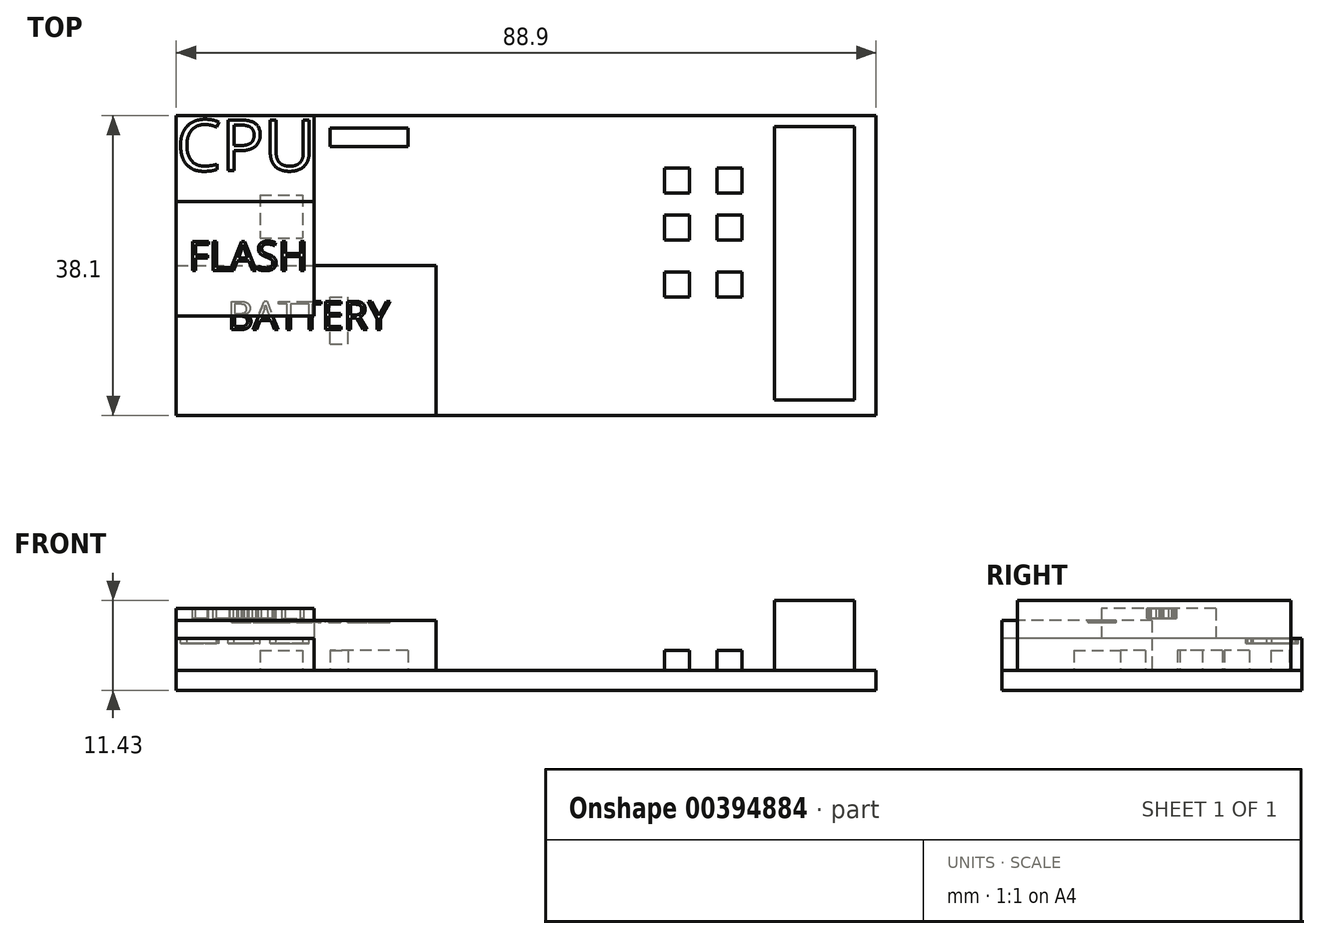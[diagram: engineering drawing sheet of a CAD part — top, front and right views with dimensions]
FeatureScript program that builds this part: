
annotation { "Feature Type Name" : "Feature", "Feature Type Description" : "" }
export const myFeature = defineFeature(function(context is Context, id is Id, definition is map)
    precondition{}
    {
        {
            var Q0;
            Q0=qCreatedBy(makeId("Top.planeOp"),FACE);
            var sketch = newSketch(context, id + "F0", { "sketchPlane" : qUnion([Q0])});
            skLineSegment(sketch, "E0.bottom", {"start": v(-84.59, -27.01) * mm, "end": v(4.31, -27.01) * mm});
            skLineSegment(sketch, "E0.top", {"start": v(-84.59, -65.11) * mm, "end": v(4.31, -65.11) * mm});
            skLineSegment(sketch, "E0.left", {"start": v(-84.59, -27.01) * mm, "end": v(-84.59, -65.11) * mm});
            skLineSegment(sketch, "E0.right", {"start": v(4.31, -27.01) * mm, "end": v(4.31, -65.11) * mm});
            skSolve(sketch);
        }
        {
            var Q0;
            Q0=makeQuery(id+"F0.imprint","IMPRINT",FACE,{"disambiguationData":[TD([[makeQuery(id+"F0.imprint","IMPRINT",EDGE,{"derivedFrom":sQuery(id+"F0.wireOp",EDGE,"E0.bottom")}),-1.0]])]});
            var sketch = newSketch(context, id + "F1", { "sketchPlane" : qUnion([Q0])});
            skLineSegment(sketch, "E1.bottom", {"start": v(-73.97, -37.1) * mm, "end": v(-68.53, -37.1) * mm});
            skLineSegment(sketch, "E1.top", {"start": v(-73.97, -42.55) * mm, "end": v(-68.53, -42.55) * mm});
            skLineSegment(sketch, "E1.left", {"start": v(-73.97, -37.1) * mm, "end": v(-73.97, -42.55) * mm});
            skLineSegment(sketch, "E1.right", {"start": v(-68.53, -37.1) * mm, "end": v(-68.53, -42.55) * mm});
            skLineSegment(sketch, "E2.bottom", {"start": v(-65.05, -56) * mm, "end": v(-62.74, -56) * mm});
            skLineSegment(sketch, "E2.top", {"start": v(-65.05, -50.1) * mm, "end": v(-62.74, -50.1) * mm});
            skLineSegment(sketch, "E2.left", {"start": v(-65.05, -56) * mm, "end": v(-65.05, -50.1) * mm});
            skLineSegment(sketch, "E2.right", {"start": v(-62.74, -56) * mm, "end": v(-62.74, -50.1) * mm});
            skLineSegment(sketch, "E3.bottom", {"start": v(-22.55, -33.7) * mm, "end": v(-19.38, -33.7) * mm});
            skLineSegment(sketch, "E3.top", {"start": v(-22.55, -36.88) * mm, "end": v(-19.38, -36.88) * mm});
            skLineSegment(sketch, "E3.left", {"start": v(-22.55, -33.7) * mm, "end": v(-22.55, -36.88) * mm});
            skLineSegment(sketch, "E3.right", {"start": v(-19.38, -33.7) * mm, "end": v(-19.38, -36.88) * mm});
            skLineSegment(sketch, "E4.bottom", {"start": v(-15.93, -36.88) * mm, "end": v(-12.75, -36.88) * mm});
            skLineSegment(sketch, "E4.top", {"start": v(-15.93, -33.7) * mm, "end": v(-12.75, -33.7) * mm});
            skLineSegment(sketch, "E4.left", {"start": v(-15.93, -36.88) * mm, "end": v(-15.93, -33.7) * mm});
            skLineSegment(sketch, "E4.right", {"start": v(-12.75, -36.88) * mm, "end": v(-12.75, -33.7) * mm});
            skLineSegment(sketch, "E5.bottom", {"start": v(-22.55, -39.69) * mm, "end": v(-19.38, -39.69) * mm});
            skLineSegment(sketch, "E5.top", {"start": v(-22.55, -42.86) * mm, "end": v(-19.38, -42.86) * mm});
            skLineSegment(sketch, "E5.left", {"start": v(-22.55, -39.69) * mm, "end": v(-22.55, -42.86) * mm});
            skLineSegment(sketch, "E5.right", {"start": v(-19.38, -39.69) * mm, "end": v(-19.38, -42.86) * mm});
            skLineSegment(sketch, "E6.bottom", {"start": v(-15.93, -42.86) * mm, "end": v(-12.75, -42.86) * mm});
            skLineSegment(sketch, "E6.top", {"start": v(-15.93, -39.69) * mm, "end": v(-12.75, -39.69) * mm});
            skLineSegment(sketch, "E6.left", {"start": v(-15.93, -42.86) * mm, "end": v(-15.93, -39.69) * mm});
            skLineSegment(sketch, "E6.right", {"start": v(-12.75, -42.86) * mm, "end": v(-12.75, -39.69) * mm});
            skLineSegment(sketch, "E7.bottom", {"start": v(-22.55, -46.92) * mm, "end": v(-19.38, -46.92) * mm});
            skLineSegment(sketch, "E7.top", {"start": v(-22.55, -50.1) * mm, "end": v(-19.38, -50.1) * mm});
            skLineSegment(sketch, "E7.left", {"start": v(-22.55, -46.92) * mm, "end": v(-22.55, -50.1) * mm});
            skLineSegment(sketch, "E7.right", {"start": v(-19.38, -46.92) * mm, "end": v(-19.38, -50.1) * mm});
            skLineSegment(sketch, "E8.bottom", {"start": v(-15.93, -46.92) * mm, "end": v(-12.75, -46.92) * mm});
            skLineSegment(sketch, "E8.top", {"start": v(-15.93, -50.1) * mm, "end": v(-12.75, -50.1) * mm});
            skLineSegment(sketch, "E8.left", {"start": v(-15.93, -46.92) * mm, "end": v(-15.93, -50.1) * mm});
            skLineSegment(sketch, "E8.right", {"start": v(-12.75, -46.92) * mm, "end": v(-12.75, -50.1) * mm});
            skPoint(sketch, "E9.oppositeSnap0", {"position": v(-65.05, -53.05) * mm});
            skLineSegment(sketch, "E9.bottom", {"start": v(-55.16, -30.95) * mm, "end": v(-65.05, -30.95) * mm});
            skLineSegment(sketch, "E9.top", {"start": v(-55.16, -28.6) * mm, "end": v(-65.05, -28.6) * mm});
            skLineSegment(sketch, "E9.left", {"start": v(-55.16, -30.95) * mm, "end": v(-55.16, -28.6) * mm});
            skLineSegment(sketch, "E9.right", {"start": v(-65.05, -30.95) * mm, "end": v(-65.05, -28.6) * mm});
            skSolve(sketch);
        }
        {
            var Q0;
            Q0 = qSketchRegion(id + "F1", true);
            extrude(context, id + "F2", {"entities" : qUnion([Q0]), "depth" : 2.54 * mm});
        }
        {
            var Q0;
            Q0 = qSketchRegion(id + "F0", true);
            extrude(context, id + "F3", {"entities" : qUnion([Q0]), "oppositeDirection" : true, "depth" : 2.54 * mm});
        }
        {
            var Q0;
            Q0=makeQuery(id+"F3.opExtrude","CAP_FACE",FACE,{"disambiguationData":[OSD([sQuery(id+"F0.wireOp",EDGE,"E0.bottom"),sQuery(id+"F0.wireOp",EDGE,"E0.top"),sQuery(id+"F0.wireOp",EDGE,"E0.left"),sQuery(id+"F0.wireOp",EDGE,"E0.right")])],"isStart":true});
            var sketch = newSketch(context, id + "F4", { "sketchPlane" : qUnion([Q0])});
            skLineSegment(sketch, "E10.bottom", {"start": v(-84.59, -46.06) * mm, "end": v(-51.6, -46.06) * mm});
            skLineSegment(sketch, "E10.top", {"start": v(-84.59, -65.11) * mm, "end": v(-51.6, -65.11) * mm});
            skLineSegment(sketch, "E10.left", {"start": v(-84.59, -46.06) * mm, "end": v(-84.59, -65.11) * mm});
            skLineSegment(sketch, "E10.right", {"start": v(-51.6, -46.06) * mm, "end": v(-51.6, -65.11) * mm});
            skSolve(sketch);
        }
        {
            var Q0;
            Q0 = qSketchRegion(id + "F4", true);
            extrude(context, id + "F5", {"entities" : qUnion([Q0]), "depth" : 6.35 * mm});
        }
        {
            var Q0;
            Q0=makeQuery(id+"F5.opExtrude","CAP_FACE",FACE,{"disambiguationData":[OSD([sQuery(id+"F4.wireOp",EDGE,"E10.bottom"),sQuery(id+"F4.wireOp",EDGE,"E10.top"),sQuery(id+"F4.wireOp",EDGE,"E10.left"),sQuery(id+"F4.wireOp",EDGE,"E10.right")])],"isStart":false});
            var sketch = newSketch(context, id + "F6", { "sketchPlane" : qUnion([Q0])});
            skText(sketch, "E11", { "text": "BATTERY", "fontName": "OpenSans-Regular.ttf"});
            const initialGuessF6  = {"E11": [-0.07806, -0.05419, 1, 0, 0.0036]};
            skSetInitialGuess(sketch, initialGuessF6);
            skSolve(sketch);
        }
        {
            var Q0;
            Q0 = qSketchRegion(id + "F6", true);
            extrude(context, id + "F7", {"entities" : qUnion([Q0]), "operationType" : NewBodyOperationType.REMOVE, "oppositeDirection" : true, "depth" : 0.25 * mm});
        }
        {
            var Q0;
            Q0=makeQuery(id+"F3.opExtrude","CAP_FACE",FACE,{"disambiguationData":[OSD([sQuery(id+"F0.wireOp",EDGE,"E0.bottom"),sQuery(id+"F0.wireOp",EDGE,"E0.top"),sQuery(id+"F0.wireOp",EDGE,"E0.left"),sQuery(id+"F0.wireOp",EDGE,"E0.right")])],"isStart":true});
            var sketch = newSketch(context, id + "F8", { "sketchPlane" : qUnion([Q0])});
            skLineSegment(sketch, "E12.bottom", {"start": v(-8.62, -28.4) * mm, "end": v(1.58, -28.4) * mm});
            skLineSegment(sketch, "E12.top", {"start": v(-8.62, -63.13) * mm, "end": v(1.58, -63.13) * mm});
            skLineSegment(sketch, "E12.left", {"start": v(-8.62, -28.4) * mm, "end": v(-8.62, -63.13) * mm});
            skLineSegment(sketch, "E12.right", {"start": v(1.58, -28.4) * mm, "end": v(1.58, -63.13) * mm});
            skSolve(sketch);
        }
        {
            var Q0;
            Q0 = qSketchRegion(id + "F8", true);
            extrude(context, id + "F9", {"entities" : qUnion([Q0]), "depth" : 8.9 * mm});
        }
        {
            var Q0;
            Q0=makeQuery(id+"F3.opExtrude","CAP_FACE",FACE,{"disambiguationData":[OSD([sQuery(id+"F0.wireOp",EDGE,"E0.bottom"),sQuery(id+"F0.wireOp",EDGE,"E0.top"),sQuery(id+"F0.wireOp",EDGE,"E0.left"),sQuery(id+"F0.wireOp",EDGE,"E0.right")])],"isStart":true});
            var sketch = newSketch(context, id + "F10", { "sketchPlane" : qUnion([Q0])});
            skLineSegment(sketch, "E13.bottom", {"start": v(-84.59, -27.01) * mm, "end": v(-67.1, -27.01) * mm});
            skLineSegment(sketch, "E13.top", {"start": v(-84.59, -65.11) * mm, "end": v(-67.1, -65.11) * mm});
            skLineSegment(sketch, "E13.left", {"start": v(-84.59, -27.01) * mm, "end": v(-84.59, -65.11) * mm});
            skLineSegment(sketch, "E13.right", {"start": v(-67.1, -27.01) * mm, "end": v(-67.1, -65.11) * mm});
            skSolve(sketch);
        }
        {
            var Q0;
            Q0 = qSketchRegion(id + "F10", true);
            extrude(context, id + "F11", {"entities" : qUnion([Q0]), "depth" : 4.06 * mm});
        }
        {
            var Q0;
            Q0=makeQuery(id+"F11.opExtrude","CAP_FACE",FACE,{"disambiguationData":[OSD([sQuery(id+"F10.wireOp",EDGE,"E13.bottom"),sQuery(id+"F10.wireOp",EDGE,"E13.top"),sQuery(id+"F10.wireOp",EDGE,"E13.left"),sQuery(id+"F10.wireOp",EDGE,"E13.right")])],"isStart":false});
            var sketch = newSketch(context, id + "F12", { "sketchPlane" : qUnion([Q0])});
            skText(sketch, "E14", { "text": "CPU", "fontName": "OpenSans-Regular.ttf"});
            const initialGuessF12  = {"E14": [-0.08459, -0.03402, 1, 0, 0.0065]};
            skSetInitialGuess(sketch, initialGuessF12);
            skSolve(sketch);
        }
        {
            var Q0;
            Q0 = qSketchRegion(id + "F12", true);
            extrude(context, id + "F13", {"entities" : qUnion([Q0]), "operationType" : NewBodyOperationType.REMOVE, "oppositeDirection" : true, "depth" : 0.64 * mm});
        }
        {
            var Q0;
            {var subQ0=sQuery(id+"F10.wireOp",EDGE,"E13.top");var subQ1=sQuery(id+"F10.wireOp",EDGE,"E13.right");var subQ2=sQuery(id+"F10.wireOp",EDGE,"E13.bottom");var subQ3=sQuery(id+"F10.wireOp",EDGE,"E13.left");Q0=makeQuery(id+"F13.boolean.opBoolean","SPLIT",FACE,{"disambiguationData":[TD([makeQuery(id+"F11.opExtrude","SWEPT_FACE",FACE,{"disambiguationData":[OSD([subQ2])]})])],"derivedFrom":makeQuery(id+"F11.opExtrude","CAP_FACE",FACE,{"disambiguationData":[OSD([subQ2,subQ0,subQ3,subQ1])],"isStart":false})});}
            var sketch = newSketch(context, id + "F14", { "sketchPlane" : qUnion([Q0])});
            skLineSegment(sketch, "E15.bottom", {"start": v(-84.59, -37.92) * mm, "end": v(-67.1, -37.92) * mm});
            skLineSegment(sketch, "E15.top", {"start": v(-84.59, -52.45) * mm, "end": v(-67.1, -52.45) * mm});
            skLineSegment(sketch, "E15.left", {"start": v(-84.59, -37.92) * mm, "end": v(-84.59, -52.45) * mm});
            skLineSegment(sketch, "E15.right", {"start": v(-67.1, -37.92) * mm, "end": v(-67.1, -52.45) * mm});
            skSolve(sketch);
        }
        {
            var Q0;
            Q0 = qSketchRegion(id + "F14", true);
            extrude(context, id + "F15", {"entities" : qUnion([Q0]), "depth" : 3.8 * mm});
        }
        {
            var Q0;
            Q0=makeQuery(id+"F15.opExtrude","CAP_FACE",FACE,{"disambiguationData":[OSD([sQuery(id+"F14.wireOp",EDGE,"E15.bottom"),sQuery(id+"F14.wireOp",EDGE,"E15.top"),sQuery(id+"F14.wireOp",EDGE,"E15.left"),sQuery(id+"F14.wireOp",EDGE,"E15.right")])],"isStart":false});
            var sketch = newSketch(context, id + "F16", { "sketchPlane" : qUnion([Q0])});
            skText(sketch, "E16", { "text": "FLASH\n", "fontName": "OpenSans-Regular.ttf"});
            const initialGuessF16  = {"E16": [-0.08304, -0.04668, 1, 0, 0.0037]};
            skSetInitialGuess(sketch, initialGuessF16);
            skSolve(sketch);
        }
        {
            var Q0;
            Q0 = qSketchRegion(id + "F16", true);
            extrude(context, id + "F17", {"entities" : qUnion([Q0]), "operationType" : NewBodyOperationType.REMOVE, "oppositeDirection" : true, "depth" : 1.27 * mm});
        }
    });
